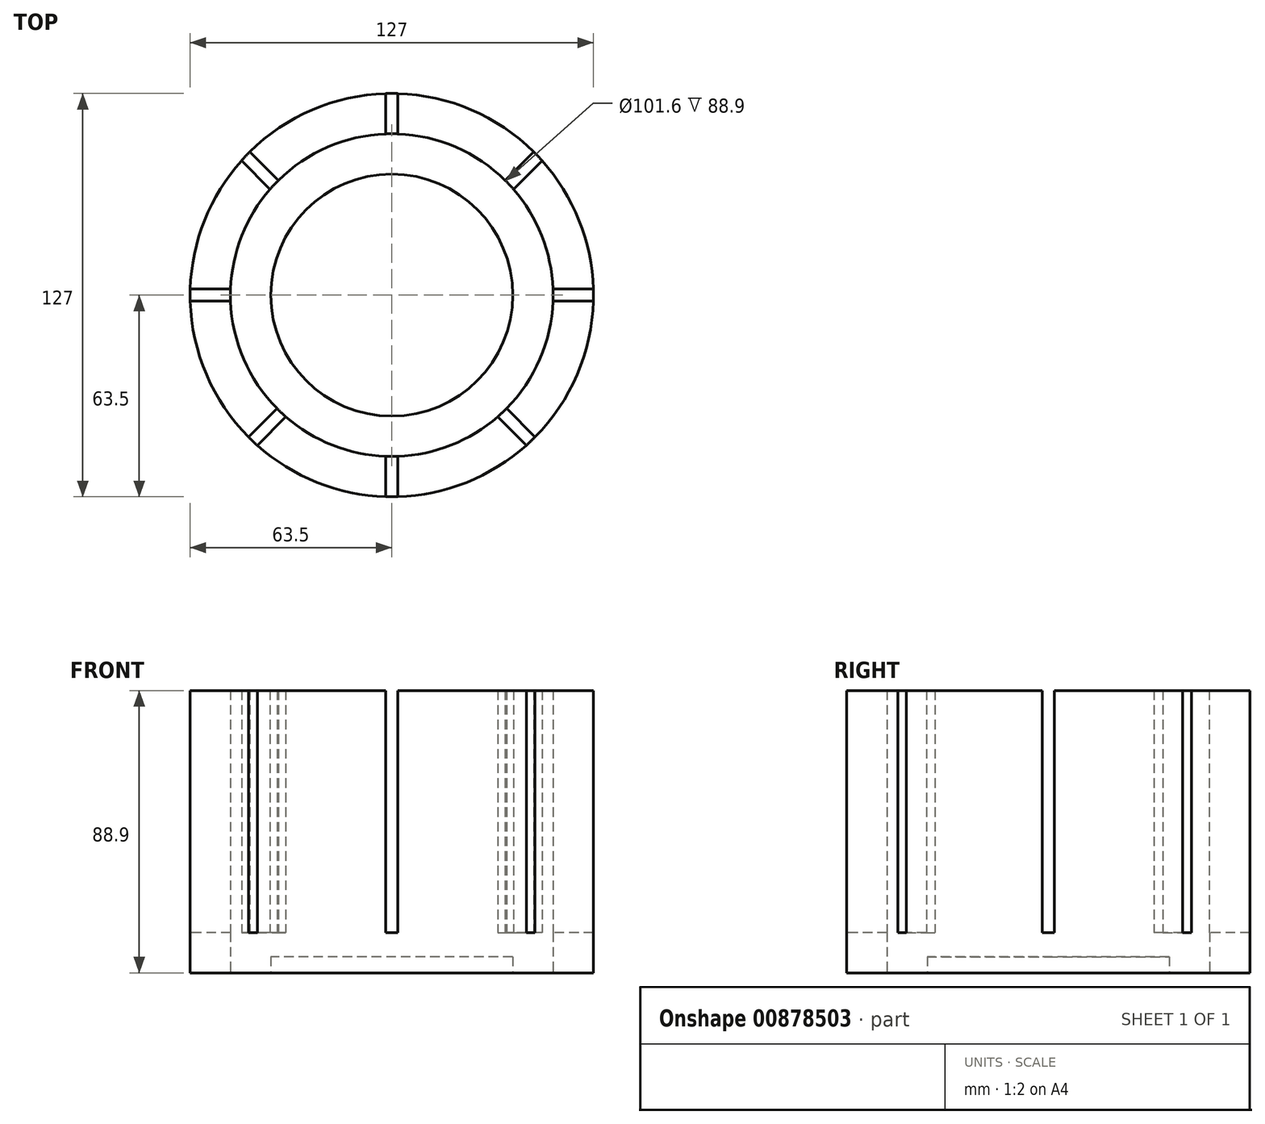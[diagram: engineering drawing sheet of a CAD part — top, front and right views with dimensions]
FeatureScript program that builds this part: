
annotation { "Feature Type Name" : "Feature", "Feature Type Description" : "" }
export const myFeature = defineFeature(function(context is Context, id is Id, definition is map)
    precondition{}
    {
        {
            var Q0;
            Q0=qCreatedBy(makeId("Top.planeOp"),FACE);
            var sketch = newSketch(context, id + "F0", { "sketchPlane" : qUnion([Q0])});
            skCircle(sketch, "E0", {"center": v(0, 0) * mm, "radius": 38.1 * mm});
            skCircle(sketch, "E1", {"center": v(0, 0) * mm, "radius": 50.8 * mm});
            skCircle(sketch, "E2", {"center": v(0, 0) * mm, "radius": 63.5 * mm});
            skSolve(sketch);
        }
        {
            var Q0;
            Q0=makeQuery(id+"F0.imprint","IMPRINT",FACE,{"disambiguationData":[TD([[makeQuery(id+"F0.imprint","IMPRINT",EDGE,{"derivedFrom":sQuery(id+"F0.wireOp",EDGE,"E1")}),-1.0]])]});
            extrude(context, id + "F1", {"entities" : qUnion([Q0]), "depth" : 88.9 * mm, "offsetDistance" : 25.4 * mm});
        }
        {
            var Q0;
            Q0=makeQuery(id+"F0.imprint","IMPRINT",FACE,{"disambiguationData":[TD([[makeQuery(id+"F0.imprint","IMPRINT",EDGE,{"derivedFrom":sQuery(id+"F0.wireOp",EDGE,"E0")}),1.0]])]});
            extrude(context, id + "F2", {"entities" : qUnion([Q0]), "operationType" : NewBodyOperationType.ADD, "depth" : 5.08 * mm, "offsetDistance" : 25.4 * mm});
        }
        {
            var Q0;
            Q0=makeQuery(id+"F1.opExtrude","CAP_FACE",FACE,{"disambiguationData":[OSD([sQuery(id+"F0.wireOp",EDGE,"E1"),sQuery(id+"F0.wireOp",EDGE,"E2")])],"isStart":false});
            var sketch = newSketch(context, id + "F3", { "sketchPlane" : qUnion([Q0])});
            skLineSegment(sketch, "E3.bottom", {"start": v(67.31, -1.9) * mm, "end": v(-67.31, -1.9) * mm});
            skLineSegment(sketch, "E3.top", {"start": v(67.31, 1.9) * mm, "end": v(-67.31, 1.9) * mm});
            skLineSegment(sketch, "E3.left", {"start": v(67.31, -1.9) * mm, "end": v(67.31, 1.9) * mm});
            skLineSegment(sketch, "E3.right", {"start": v(-67.31, -1.9) * mm, "end": v(-67.31, 1.9) * mm});
            skPoint(sketch, "E3.middle", {"position": v(0, 0) * mm});
            skLineSegment(sketch, "E4.bottom", {"start": v(-1.9, 67.31) * mm, "end": v(1.9, 67.31) * mm});
            skLineSegment(sketch, "E4.top", {"start": v(-1.9, -67.31) * mm, "end": v(1.9, -67.31) * mm});
            skLineSegment(sketch, "E4.left", {"start": v(-1.9, 67.31) * mm, "end": v(-1.9, -67.31) * mm});
            skLineSegment(sketch, "E4.right", {"start": v(1.9, 67.31) * mm, "end": v(1.9, -67.31) * mm});
            skLineSegment(sketch, "E5", {"start": v(1.9, 2.33) * mm, "end": v(48.37, 48.8) * mm});
            skLineSegment(sketch, "E6", {"start": v(48.37, 48.8) * mm, "end": v(51.07, 46.1) * mm});
            skLineSegment(sketch, "E7", {"start": v(51.07, 46.1) * mm, "end": v(6.87, 1.9) * mm});
            skLineSegment(sketch, "E8", {"start": v(6.87, 1.9) * mm, "end": v(-44.7, -49.66) * mm});
            skLineSegment(sketch, "E9", {"start": v(-44.7, -49.66) * mm, "end": v(-47.4, -46.97) * mm});
            skLineSegment(sketch, "E10", {"start": v(-47.4, -46.97) * mm, "end": v(-2.33, -1.9) * mm});
            skLineSegment(sketch, "E11", {"start": v(-2.33, -1.9) * mm, "end": v(1.9, 2.33) * mm});
            skLineSegment(sketch, "E12", {"start": v(-1.9, 2.33) * mm, "end": v(-47.57, 48) * mm});
            skLineSegment(sketch, "E13", {"start": v(-47.57, 48) * mm, "end": v(-50.27, 45.3) * mm});
            skLineSegment(sketch, "E14", {"start": v(-50.27, 45.3) * mm, "end": v(-6.87, 1.9) * mm});
            skLineSegment(sketch, "E15", {"start": v(-6.87, 1.9) * mm, "end": v(49.32, -54.28) * mm});
            skLineSegment(sketch, "E16", {"start": v(49.32, -54.28) * mm, "end": v(52.02, -51.59) * mm});
            skLineSegment(sketch, "E17", {"start": v(52.02, -51.59) * mm, "end": v(2.33, -1.9) * mm});
            skLineSegment(sketch, "E18", {"start": v(-1.9, 2.33) * mm, "end": v(2.33, -1.9) * mm});
            skSolve(sketch);
        }
        {
            var Q0;
            {var subQ0=sQuery(id+"F3.wireOp",EDGE,"E15");var subQ1=sQuery(id+"F3.wireOp",EDGE,"E4.left");var subQ2=makeQuery(id+"F3.imprint","INTERSECT",VERTEX,{"derivedFrom":[subQ1,subQ0]});Q0=makeQuery(id+"F3.imprint","IMPRINT",FACE,{"disambiguationData":[TD([[makeQuery(id+"F3.imprint","IMPRINT",EDGE,{"disambiguationData":[TD([[subQ2,-1.0]])],"derivedFrom":subQ1}),-1.0]])]});}
            var Q1;
            {var subQ0=sQuery(id+"F3.wireOp",EDGE,"E8");var subQ1=makeQuery(id+"F1.opExtrude","CAP_EDGE",EDGE,{"disambiguationData":[OSD([sQuery(id+"F0.wireOp",EDGE,"E2")])],"isStart":false});var subQ2=makeQuery(id+"F3.imprint","INTERSECT",VERTEX,{"derivedFrom":[subQ1,subQ0]});Q1=makeQuery(id+"F3.imprint","IMPRINT",FACE,{"disambiguationData":[TD([[makeQuery(id+"F3.imprint","IMPRINT",EDGE,{"disambiguationData":[TD([[subQ2,1.0]])],"derivedFrom":subQ0}),-1.0]])]});}
            var Q2;
            {var subQ0=sQuery(id+"F3.wireOp",EDGE,"E9");Q2=makeQuery(id+"F3.imprint","IMPRINT",FACE,{"disambiguationData":[TD([[makeQuery(id+"F3.imprint","IMPRINT",EDGE,{"derivedFrom":subQ0}),-1.0]])]});}
            var Q3;
            {var subQ0=sQuery(id+"F3.wireOp",EDGE,"E3.right");Q3=makeQuery(id+"F3.imprint","IMPRINT",FACE,{"disambiguationData":[TD([[makeQuery(id+"F3.imprint","IMPRINT",EDGE,{"derivedFrom":subQ0}),-1.0]])]});}
            var Q4;
            {var subQ0=sQuery(id+"F3.wireOp",EDGE,"E3.bottom");var subQ1=makeQuery(id+"F1.opExtrude","CAP_EDGE",EDGE,{"disambiguationData":[OSD([sQuery(id+"F0.wireOp",EDGE,"E2")])],"isStart":false});var subQ2=makeQuery(id+"F3.imprint","INTERSECT",VERTEX,{"disambiguationData":[OD(1.0)],"derivedFrom":[subQ1,subQ0]});Q4=makeQuery(id+"F3.imprint","IMPRINT",FACE,{"disambiguationData":[TD([[makeQuery(id+"F3.imprint","IMPRINT",EDGE,{"disambiguationData":[TD([[subQ2,1.0]])],"derivedFrom":subQ0}),-1.0]])]});}
            var Q5;
            {var subQ0=sQuery(id+"F3.wireOp",EDGE,"E15");var subQ1=sQuery(id+"F3.wireOp",EDGE,"E3.bottom");var subQ2=makeQuery(id+"F3.imprint","INTERSECT",VERTEX,{"derivedFrom":[subQ1,subQ0]});Q5=makeQuery(id+"F3.imprint","IMPRINT",FACE,{"disambiguationData":[TD([[makeQuery(id+"F3.imprint","IMPRINT",EDGE,{"disambiguationData":[TD([[subQ2,-1.0]])],"derivedFrom":subQ1}),-1.0]])]});}
            var Q6;
            {var subQ0=sQuery(id+"F3.wireOp",EDGE,"E12");var subQ3=makeQuery(id+"F1.opExtrude","CAP_EDGE",EDGE,{"disambiguationData":[OSD([sQuery(id+"F0.wireOp",EDGE,"E1")])],"isStart":false});var subQ4=makeQuery(id+"F3.imprint","INTERSECT",VERTEX,{"derivedFrom":[subQ3,subQ0]});Q6=makeQuery(id+"F3.imprint","IMPRINT",FACE,{"disambiguationData":[TD([[makeQuery(id+"F3.imprint","IMPRINT",EDGE,{"disambiguationData":[TD([[subQ4,-1.0]])],"derivedFrom":subQ3}),1.0]])]});}
            var Q7;
            {var subQ0=sQuery(id+"F3.wireOp",EDGE,"E5");var subQ3=makeQuery(id+"F1.opExtrude","CAP_EDGE",EDGE,{"disambiguationData":[OSD([sQuery(id+"F0.wireOp",EDGE,"E1")])],"isStart":false});var subQ4=makeQuery(id+"F3.imprint","INTERSECT",VERTEX,{"derivedFrom":[subQ3,subQ0]});Q7=makeQuery(id+"F3.imprint","IMPRINT",FACE,{"disambiguationData":[TD([[makeQuery(id+"F3.imprint","IMPRINT",EDGE,{"disambiguationData":[TD([[subQ4,1.0]])],"derivedFrom":subQ3}),1.0]])]});}
            var Q8;
            {var subQ0=sQuery(id+"F3.wireOp",EDGE,"E8");var subQ1=sQuery(id+"F3.wireOp",EDGE,"E3.bottom");var subQ2=makeQuery(id+"F3.imprint","INTERSECT",VERTEX,{"derivedFrom":[subQ1,subQ0]});Q8=makeQuery(id+"F3.imprint","IMPRINT",FACE,{"disambiguationData":[TD([[makeQuery(id+"F3.imprint","IMPRINT",EDGE,{"disambiguationData":[TD([[subQ2,1.0]])],"derivedFrom":subQ1}),-1.0]])]});}
            var Q9;
            {var subQ0=sQuery(id+"F3.wireOp",EDGE,"E3.bottom");var subQ1=makeQuery(id+"F1.opExtrude","CAP_EDGE",EDGE,{"disambiguationData":[OSD([sQuery(id+"F0.wireOp",EDGE,"E2")])],"isStart":false});var subQ2=makeQuery(id+"F3.imprint","INTERSECT",VERTEX,{"disambiguationData":[OD(0.0)],"derivedFrom":[subQ1,subQ0]});Q9=makeQuery(id+"F3.imprint","IMPRINT",FACE,{"disambiguationData":[TD([[makeQuery(id+"F3.imprint","IMPRINT",EDGE,{"disambiguationData":[TD([[subQ2,-1.0]])],"derivedFrom":subQ0}),-1.0]])]});}
            var Q10;
            {var subQ0=sQuery(id+"F3.wireOp",EDGE,"E5");var subQ1=makeQuery(id+"F1.opExtrude","CAP_EDGE",EDGE,{"disambiguationData":[OSD([sQuery(id+"F0.wireOp",EDGE,"E2")])],"isStart":false});var subQ2=makeQuery(id+"F3.imprint","INTERSECT",VERTEX,{"derivedFrom":[subQ1,subQ0]});Q10=makeQuery(id+"F3.imprint","IMPRINT",FACE,{"disambiguationData":[TD([[makeQuery(id+"F3.imprint","IMPRINT",EDGE,{"disambiguationData":[TD([[subQ2,1.0]])],"derivedFrom":subQ0}),-1.0]])]});}
            var Q11;
            {var subQ1=sQuery(id+"F3.wireOp",EDGE,"E8");var subQ5=sQuery(id+"F3.wireOp",EDGE,"E4.right");var subQ6=makeQuery(id+"F3.imprint","INTERSECT",VERTEX,{"derivedFrom":[subQ5,subQ1]});Q11=makeQuery(id+"F3.imprint","IMPRINT",FACE,{"disambiguationData":[TD([[makeQuery(id+"F3.imprint","IMPRINT",EDGE,{"disambiguationData":[TD([[subQ6,-1.0]])],"derivedFrom":subQ5}),1.0]])]});}
            var Q12;
            {var subQ0=sQuery(id+"F3.wireOp",EDGE,"E15");var subQ1=makeQuery(id+"F1.opExtrude","CAP_EDGE",EDGE,{"disambiguationData":[OSD([sQuery(id+"F0.wireOp",EDGE,"E2")])],"isStart":false});var subQ2=makeQuery(id+"F3.imprint","INTERSECT",VERTEX,{"derivedFrom":[subQ1,subQ0]});Q12=makeQuery(id+"F3.imprint","IMPRINT",FACE,{"disambiguationData":[TD([[makeQuery(id+"F3.imprint","IMPRINT",EDGE,{"disambiguationData":[TD([[subQ2,1.0]])],"derivedFrom":subQ0}),1.0]])]});}
            var Q13;
            {var subQ0=sQuery(id+"F3.wireOp",EDGE,"E16");Q13=makeQuery(id+"F3.imprint","IMPRINT",FACE,{"disambiguationData":[TD([[makeQuery(id+"F3.imprint","IMPRINT",EDGE,{"derivedFrom":subQ0}),1.0]])]});}
            var Q14;
            {var subQ0=sQuery(id+"F3.wireOp",EDGE,"E3.left");Q14=makeQuery(id+"F3.imprint","IMPRINT",FACE,{"disambiguationData":[TD([[makeQuery(id+"F3.imprint","IMPRINT",EDGE,{"derivedFrom":subQ0}),1.0]])]});}
            var Q15;
            {var subQ0=sQuery(id+"F3.wireOp",EDGE,"E6");Q15=makeQuery(id+"F3.imprint","IMPRINT",FACE,{"disambiguationData":[TD([[makeQuery(id+"F3.imprint","IMPRINT",EDGE,{"derivedFrom":subQ0}),-1.0]])]});}
            var Q16;
            {var subQ0=sQuery(id+"F3.wireOp",EDGE,"E12");var subQ1=makeQuery(id+"F1.opExtrude","CAP_EDGE",EDGE,{"disambiguationData":[OSD([sQuery(id+"F0.wireOp",EDGE,"E2")])],"isStart":false});var subQ2=makeQuery(id+"F3.imprint","INTERSECT",VERTEX,{"derivedFrom":[subQ1,subQ0]});Q16=makeQuery(id+"F3.imprint","IMPRINT",FACE,{"disambiguationData":[TD([[makeQuery(id+"F3.imprint","IMPRINT",EDGE,{"disambiguationData":[TD([[subQ2,1.0]])],"derivedFrom":subQ0}),1.0]])]});}
            var Q17;
            {var subQ0=sQuery(id+"F3.wireOp",EDGE,"E11");var subQ9=sQuery(id+"F3.wireOp",EDGE,"E3.top");var subQ10=makeQuery(id+"F3.imprint","INTERSECT",VERTEX,{"derivedFrom":[subQ9,subQ0]});Q17=makeQuery(id+"F3.imprint","IMPRINT",FACE,{"disambiguationData":[TD([[makeQuery(id+"F3.imprint","IMPRINT",EDGE,{"disambiguationData":[TD([[subQ10,-1.0]])],"derivedFrom":subQ9}),-1.0]])]});}
            var Q18;
            {var subQ0=sQuery(id+"F3.wireOp",EDGE,"E4.left");var subQ1=makeQuery(id+"F1.opExtrude","CAP_EDGE",EDGE,{"disambiguationData":[OSD([sQuery(id+"F0.wireOp",EDGE,"E2")])],"isStart":false});var subQ2=makeQuery(id+"F3.imprint","INTERSECT",VERTEX,{"disambiguationData":[OD(0.0)],"derivedFrom":[subQ1,subQ0]});Q18=makeQuery(id+"F3.imprint","IMPRINT",FACE,{"disambiguationData":[TD([[makeQuery(id+"F3.imprint","IMPRINT",EDGE,{"disambiguationData":[TD([[subQ2,-1.0]])],"derivedFrom":subQ0}),1.0]])]});}
            var Q19;
            {var subQ0=sQuery(id+"F3.wireOp",EDGE,"E13");Q19=makeQuery(id+"F3.imprint","IMPRINT",FACE,{"disambiguationData":[TD([[makeQuery(id+"F3.imprint","IMPRINT",EDGE,{"derivedFrom":subQ0}),1.0]])]});}
            var Q20;
            {var subQ0=sQuery(id+"F3.wireOp",EDGE,"E4.bottom");Q20=makeQuery(id+"F3.imprint","IMPRINT",FACE,{"disambiguationData":[TD([[makeQuery(id+"F3.imprint","IMPRINT",EDGE,{"derivedFrom":subQ0}),-1.0]])]});}
            var Q21;
            {var subQ0=sQuery(id+"F3.wireOp",EDGE,"E4.left");var subQ1=makeQuery(id+"F1.opExtrude","CAP_EDGE",EDGE,{"disambiguationData":[OSD([sQuery(id+"F0.wireOp",EDGE,"E2")])],"isStart":false});var subQ2=makeQuery(id+"F3.imprint","INTERSECT",VERTEX,{"disambiguationData":[OD(1.0)],"derivedFrom":[subQ1,subQ0]});Q21=makeQuery(id+"F3.imprint","IMPRINT",FACE,{"disambiguationData":[TD([[makeQuery(id+"F3.imprint","IMPRINT",EDGE,{"disambiguationData":[TD([[subQ2,1.0]])],"derivedFrom":subQ0}),1.0]])]});}
            var Q22;
            {var subQ3=sQuery(id+"F3.wireOp",EDGE,"E8");var subQ7=sQuery(id+"F3.wireOp",EDGE,"E4.left");var subQ8=makeQuery(id+"F3.imprint","INTERSECT",VERTEX,{"derivedFrom":[subQ7,subQ3]});Q22=makeQuery(id+"F3.imprint","IMPRINT",FACE,{"disambiguationData":[TD([[makeQuery(id+"F3.imprint","IMPRINT",EDGE,{"disambiguationData":[TD([[subQ8,-1.0]])],"derivedFrom":subQ7}),1.0]])]});}
            extrude(context, id + "F4", {"entities" : qUnion([Q0, Q1, Q2, Q3, Q4, Q5, Q6, Q7, Q8, Q9, Q10, Q11, Q12, Q13, Q14, Q15, Q16, Q17, Q18, Q19, Q20, Q21, Q22]), "operationType" : NewBodyOperationType.REMOVE, "oppositeDirection" : true, "depth" : 76.2 * mm, "offsetDistance" : 25.4 * mm});
        }
    });
